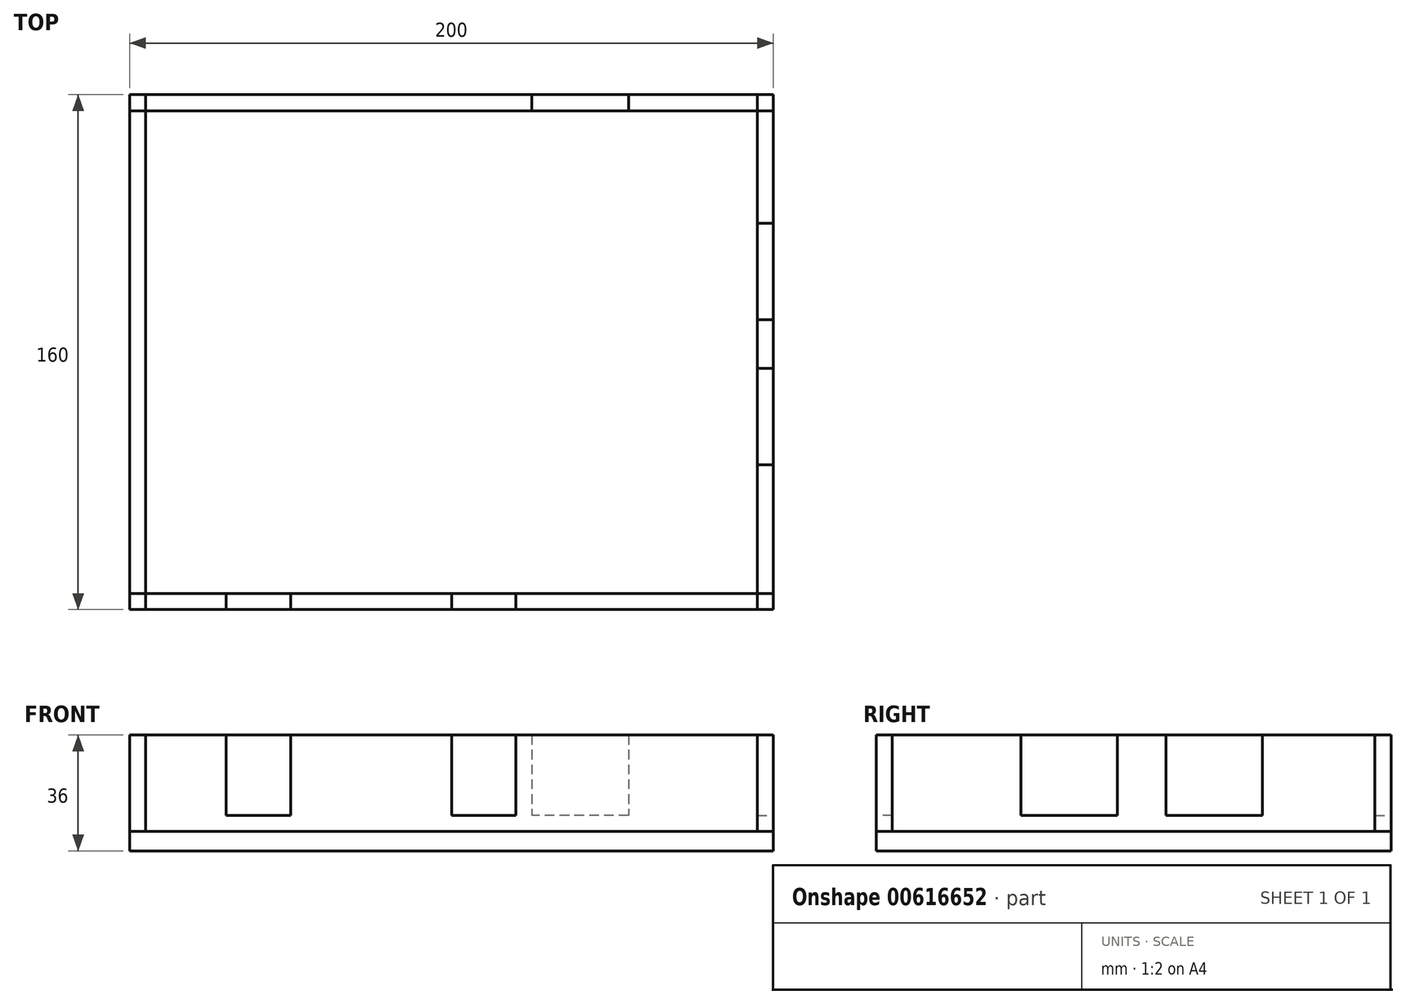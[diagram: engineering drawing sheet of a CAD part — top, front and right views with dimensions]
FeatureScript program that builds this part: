
annotation { "Feature Type Name" : "Feature", "Feature Type Description" : "" }
export const myFeature = defineFeature(function(context is Context, id is Id, definition is map)
    precondition{}
    {
        {
            var Q0;
            Q0=qCreatedBy(makeId("Top.planeOp"),FACE);
            var sketch = newSketch(context, id + "F0", { "sketchPlane" : qUnion([Q0])});
            skLineSegment(sketch, "E0.bottom", {"start": v(-81.94, -85.75) * mm, "end": v(118.06, -85.75) * mm});
            skLineSegment(sketch, "E0.top", {"start": v(-81.94, 74.25) * mm, "end": v(118.06, 74.25) * mm});
            skLineSegment(sketch, "E0.left", {"start": v(-81.94, -85.75) * mm, "end": v(-81.94, 74.25) * mm});
            skLineSegment(sketch, "E0.right", {"start": v(118.06, -85.75) * mm, "end": v(118.06, 74.25) * mm});
            skSolve(sketch);
        }
        {
            var Q0;
            Q0=makeQuery(id+"F0.imprint","IMPRINT",FACE,{"disambiguationData":[TD([[makeQuery(id+"F0.imprint","IMPRINT",EDGE,{"derivedFrom":sQuery(id+"F0.wireOp",EDGE,"E0.bottom")}),1.0]])]});
            extrude(context, id + "F1", {"entities" : qUnion([Q0]), "depth" : 6 * mm, "offsetDistance" : 25 * mm});
        }
        {
            var Q0;
            Q0=makeQuery(id+"F1.opExtrude","CAP_FACE",FACE,{"disambiguationData":[OSD([sQuery(id+"F0.wireOp",EDGE,"E0.bottom"),sQuery(id+"F0.wireOp",EDGE,"E0.top"),sQuery(id+"F0.wireOp",EDGE,"E0.left"),sQuery(id+"F0.wireOp",EDGE,"E0.right")])],"isStart":false});
            var sketch = newSketch(context, id + "F2", { "sketchPlane" : qUnion([Q0])});
            skLineSegment(sketch, "E1.bottom", {"start": v(-81.94, 74.25) * mm, "end": v(118.06, 74.25) * mm});
            skLineSegment(sketch, "E1.top", {"start": v(-81.94, 69.25) * mm, "end": v(118.06, 69.25) * mm});
            skLineSegment(sketch, "E1.left", {"start": v(-81.94, 74.25) * mm, "end": v(-81.94, 69.25) * mm});
            skLineSegment(sketch, "E1.right", {"start": v(118.06, 74.25) * mm, "end": v(118.06, 69.25) * mm});
            skSolve(sketch);
        }
        {
            var Q0;
            Q0=qSketchRegion(id+"F2",true);
            extrude(context, id + "F3", {"entities" : qUnion([Q0]), "depth" : 30 * mm, "offsetDistance" : 25 * mm});
        }
        {
            var Q0;
            Q0=makeQuery(id+"F1.opExtrude","CAP_FACE",FACE,{"disambiguationData":[OSD([sQuery(id+"F0.wireOp",EDGE,"E0.bottom"),sQuery(id+"F0.wireOp",EDGE,"E0.top"),sQuery(id+"F0.wireOp",EDGE,"E0.left"),sQuery(id+"F0.wireOp",EDGE,"E0.right")])],"isStart":false});
            var sketch = newSketch(context, id + "F4", { "sketchPlane" : qUnion([Q0])});
            skLineSegment(sketch, "E2.bottom", {"start": v(-81.94, 74.25) * mm, "end": v(-76.94, 74.25) * mm});
            skLineSegment(sketch, "E2.top", {"start": v(-81.94, -85.75) * mm, "end": v(-76.94, -85.75) * mm});
            skLineSegment(sketch, "E2.left", {"start": v(-81.94, 74.25) * mm, "end": v(-81.94, -85.75) * mm});
            skLineSegment(sketch, "E2.right", {"start": v(-76.94, 74.25) * mm, "end": v(-76.94, -85.75) * mm});
            skSolve(sketch);
        }
        {
            var Q0;
            Q0=qSketchRegion(id+"F4",true);
            extrude(context, id + "F5", {"entities" : qUnion([Q0]), "depth" : 30 * mm, "offsetDistance" : 25 * mm});
        }
        {
            var Q0;
            Q0=makeQuery(id+"F1.opExtrude","CAP_FACE",FACE,{"disambiguationData":[OSD([sQuery(id+"F0.wireOp",EDGE,"E0.bottom"),sQuery(id+"F0.wireOp",EDGE,"E0.top"),sQuery(id+"F0.wireOp",EDGE,"E0.left"),sQuery(id+"F0.wireOp",EDGE,"E0.right")])],"isStart":false});
            var sketch = newSketch(context, id + "F6", { "sketchPlane" : qUnion([Q0])});
            skLineSegment(sketch, "E3.bottom", {"start": v(-81.94, -85.75) * mm, "end": v(118.06, -85.75) * mm});
            skLineSegment(sketch, "E3.top", {"start": v(-81.94, -80.75) * mm, "end": v(118.06, -80.75) * mm});
            skLineSegment(sketch, "E3.left", {"start": v(-81.94, -85.75) * mm, "end": v(-81.94, -80.75) * mm});
            skLineSegment(sketch, "E3.right", {"start": v(118.06, -85.75) * mm, "end": v(118.06, -80.75) * mm});
            skSolve(sketch);
        }
        {
            var Q0;
            Q0=qSketchRegion(id+"F6",true);
            extrude(context, id + "F7", {"entities" : qUnion([Q0]), "depth" : 30 * mm, "offsetDistance" : 25 * mm});
        }
        {
            var Q0;
            Q0=makeQuery(id+"F7.opExtrude","SWEPT_FACE",FACE,{"disambiguationData":[OSD([sQuery(id+"F6.wireOp",EDGE,"E3.bottom")])]});
            var sketch = newSketch(context, id + "F8", { "sketchPlane" : qUnion([Q0])});
            skLineSegment(sketch, "E4.bottom", {"start": v(-51.94, 36) * mm, "end": v(-31.94, 36) * mm});
            skLineSegment(sketch, "E4.top", {"start": v(-51.94, 11) * mm, "end": v(-31.94, 11) * mm});
            skLineSegment(sketch, "E4.left", {"start": v(-51.94, 36) * mm, "end": v(-51.94, 11) * mm});
            skLineSegment(sketch, "E4.right", {"start": v(-31.94, 36) * mm, "end": v(-31.94, 11) * mm});
            skSolve(sketch);
        }
        {
            var Q0;
            Q0=qSketchRegion(id+"F8",true);
            extrude(context, id + "F9", {"entities" : qUnion([Q0]), "operationType" : NewBodyOperationType.REMOVE, "oppositeDirection" : true, "depth" : 25 * mm, "offsetDistance" : 25 * mm});
        }
        {
            var Q0;
            Q0=makeQuery(id+"F7.opExtrude","SWEPT_FACE",FACE,{"disambiguationData":[OSD([sQuery(id+"F6.wireOp",EDGE,"E3.bottom")])]});
            var sketch = newSketch(context, id + "F10", { "sketchPlane" : qUnion([Q0])});
            skLineSegment(sketch, "E5.bottom", {"start": v(38.06, 36) * mm, "end": v(18.06, 36) * mm});
            skLineSegment(sketch, "E5.top", {"start": v(38.06, 11) * mm, "end": v(18.06, 11) * mm});
            skLineSegment(sketch, "E5.left", {"start": v(38.06, 36) * mm, "end": v(38.06, 11) * mm});
            skLineSegment(sketch, "E5.right", {"start": v(18.06, 36) * mm, "end": v(18.06, 11) * mm});
            skSolve(sketch);
        }
        {
            var Q0;
            Q0=qSketchRegion(id+"F10",true);
            extrude(context, id + "F11", {"entities" : qUnion([Q0]), "operationType" : NewBodyOperationType.REMOVE, "oppositeDirection" : true, "depth" : 25 * mm, "offsetDistance" : 25 * mm});
        }
        {
            var Q0;
            Q0=makeQuery(id+"F1.opExtrude","CAP_FACE",FACE,{"disambiguationData":[OSD([sQuery(id+"F0.wireOp",EDGE,"E0.bottom"),sQuery(id+"F0.wireOp",EDGE,"E0.top"),sQuery(id+"F0.wireOp",EDGE,"E0.left"),sQuery(id+"F0.wireOp",EDGE,"E0.right")])],"isStart":false});
            var sketch = newSketch(context, id + "F12", { "sketchPlane" : qUnion([Q0])});
            skLineSegment(sketch, "E6.bottom", {"start": v(113.06, 74.25) * mm, "end": v(118.06, 74.25) * mm});
            skLineSegment(sketch, "E6.top", {"start": v(113.06, -85.75) * mm, "end": v(118.06, -85.75) * mm});
            skLineSegment(sketch, "E6.left", {"start": v(113.06, 74.25) * mm, "end": v(113.06, -85.75) * mm});
            skLineSegment(sketch, "E6.right", {"start": v(118.06, 74.25) * mm, "end": v(118.06, -85.75) * mm});
            skSolve(sketch);
        }
        {
            var Q0;
            Q0=qSketchRegion(id+"F12",true);
            extrude(context, id + "F13", {"entities" : qUnion([Q0]), "depth" : 30 * mm, "offsetDistance" : 25 * mm});
        }
        {
            var Q0;
            Q0=makeQuery(id+"F13.opExtrude","SWEPT_FACE",FACE,{"disambiguationData":[OSD([sQuery(id+"F12.wireOp",EDGE,"E6.right")])]});
            var sketch = newSketch(context, id + "F14", { "sketchPlane" : qUnion([Q0])});
            skLineSegment(sketch, "E7.bottom", {"start": v(-40.75, 36) * mm, "end": v(-10.75, 36) * mm});
            skLineSegment(sketch, "E7.top", {"start": v(-40.75, 11) * mm, "end": v(-10.75, 11) * mm});
            skLineSegment(sketch, "E7.left", {"start": v(-40.75, 36) * mm, "end": v(-40.75, 11) * mm});
            skLineSegment(sketch, "E7.right", {"start": v(-10.75, 36) * mm, "end": v(-10.75, 11) * mm});
            skSolve(sketch);
        }
        {
            var Q0;
            Q0=qSketchRegion(id+"F14",true);
            extrude(context, id + "F15", {"entities" : qUnion([Q0]), "operationType" : NewBodyOperationType.REMOVE, "oppositeDirection" : true, "depth" : 25 * mm, "offsetDistance" : 25 * mm});
        }
        {
            var Q0;
            Q0=makeQuery(id+"F13.opExtrude","SWEPT_FACE",FACE,{"disambiguationData":[OSD([sQuery(id+"F12.wireOp",EDGE,"E6.right")])]});
            var sketch = newSketch(context, id + "F16", { "sketchPlane" : qUnion([Q0])});
            skLineSegment(sketch, "E8.bottom", {"start": v(4.25, 36) * mm, "end": v(34.25, 36) * mm});
            skLineSegment(sketch, "E8.top", {"start": v(4.25, 11) * mm, "end": v(34.25, 11) * mm});
            skLineSegment(sketch, "E8.left", {"start": v(4.25, 36) * mm, "end": v(4.25, 11) * mm});
            skLineSegment(sketch, "E8.right", {"start": v(34.25, 36) * mm, "end": v(34.25, 11) * mm});
            skSolve(sketch);
        }
        {
            var Q0;
            Q0=qSketchRegion(id+"F16",true);
            extrude(context, id + "F17", {"entities" : qUnion([Q0]), "operationType" : NewBodyOperationType.REMOVE, "oppositeDirection" : true, "depth" : 25 * mm, "offsetDistance" : 25 * mm});
        }
        {
            var Q0;
            Q0=makeQuery(id+"F3.opExtrude","SWEPT_FACE",FACE,{"disambiguationData":[OSD([sQuery(id+"F2.wireOp",EDGE,"E1.bottom")])]});
            var sketch = newSketch(context, id + "F18", { "sketchPlane" : qUnion([Q0])});
            skLineSegment(sketch, "E9.bottom", {"start": v(-73.06, 36) * mm, "end": v(-43.06, 36) * mm});
            skLineSegment(sketch, "E9.top", {"start": v(-73.06, 11) * mm, "end": v(-43.06, 11) * mm});
            skLineSegment(sketch, "E9.left", {"start": v(-73.06, 36) * mm, "end": v(-73.06, 11) * mm});
            skLineSegment(sketch, "E9.right", {"start": v(-43.06, 36) * mm, "end": v(-43.06, 11) * mm});
            skSolve(sketch);
        }
        {
            var Q0;
            Q0=qSketchRegion(id+"F18",true);
            extrude(context, id + "F19", {"entities" : qUnion([Q0]), "operationType" : NewBodyOperationType.REMOVE, "oppositeDirection" : true, "depth" : 25 * mm, "offsetDistance" : 25 * mm});
        }
    });
